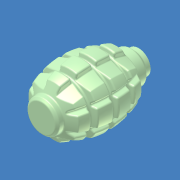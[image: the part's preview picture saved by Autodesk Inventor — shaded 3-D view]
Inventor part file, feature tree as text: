
AUTODESK INVENTOR PART (.ipt)
format: ipt  version: 2011 SP1 (Build 150282100, 282)  size: 2,516,992 bytes
history: native  units: mm (DEFAULTED — no unit token found)
features: sketch x7, revolve x3, other x2, mirror x2, extrude x2, fillet x2, hole x2
ambient origin geometry x8: Origin, YZ Plane, XZ Plane, XY Plane, X Axis, Y Axis, Z Axis, Center Point
feature tree (20):
  other  "Твердое тело1"
  revolve  "Вращение1"
  other  "РабПлоскость1"
  revolve  "Вращение2"
  revolve  "Вращение3"
  mirror  "ЗеркОтобр1"
  mirror  "ЗеркОтобр2"
  extrude  "Выдавливание1"  Depth=27.5mm
  fillet  "Сопряжение2"  Radius=85.0mm
  extrude  "Выдавливание2"  Depth=14.0mm
  hole  "Отверстие1"  [1 undecoded]
  hole  "Отверстие2"  [1 undecoded]
  fillet  "Сопряжение3"  Radius=2.0mm
  sketch  "Эскиз1"
  sketch  "Эскиз2"
  sketch  "Эскиз3"
  sketch  "Эскиз4"
  sketch  "Эскиз5"
  sketch  "Эскиз6"
  sketch  "Эскиз7"
note: 2 required parameter values undecoded (feature->parameter linkage not recoverable at this tier; creation-order binding heuristic only, values carry confidence <= 0.55)
